# Revit family: Panneaux modulaires 19 pouces à équiper de cassettes
name_source: partatom
category: Installations électriques
units: mm (PartAtom-declared; Revit-internal decimal feet)

## family parameters
Basée sur le plan de construction = Non
Conserver l'orientation des annotations = Non
Cote de connecteur circulaire = Utiliser le diamètre
Couper avec des vides une fois chargée = Non
Partagée = Non
Point de calcul de pièce = Non
Toujours verticalement = Oui
Type d'élément = Normal

## types (3) — shared parameters
Avec boîtier = Non
Avec façade = Non
Avec pigtails = Non
Classe ETIM = EC001130
Fonction = Panneaux fibre optique HD 19 pouces à équiper
IK = IK05
Largeur (mm) = 483 mm
Lien e-catalogue = https://www.legrand.fr
Mode de pose = Encastrement 19 pouces
Préconnecté = Non
Température de fonctionnement = -30°C à 60°C
Température de stockage = -30°C à 60°C
zero-valued in all types: Elévation par défaut

## per-type parameters (varying)
| type | Avec porte-étiquette | EAN | Hauteur | Management arrière | Management avant | Nombre d'unités | Profondeur | Référence Legrand | Type de management avant |
| Panneau modulaire HD 1U à équiper | Non | 3414971929173 | 44 mm  [stored 0.144357 ft] | Non | Non | 1 | 201 mm  [stored 0.659449 ft] | 032175 | Management avant : 2U |
| Panneau modulaire HD 2U à équiper | Oui | 3414971929180 | 89 mm  [stored 0.291995 ft] | Oui | Oui | 2 | 492 mm  [stored 1.61417 ft] | 032176 | Management avant : 2U |
| Panneau modulaire HD 4U à équiper | Oui | 3414971929197 | 178 mm  [stored 0.58399 ft] | Oui | Oui | 4 | 492 mm  [stored 1.61417 ft] | 032177 | Management avant : 4U |

note: column(s) folded — value = type name in every type: Libellé BIM

note: [stored X ft] marks values corroborated as IEEE doubles in the binary element streams (Revit-internal decimal feet)
